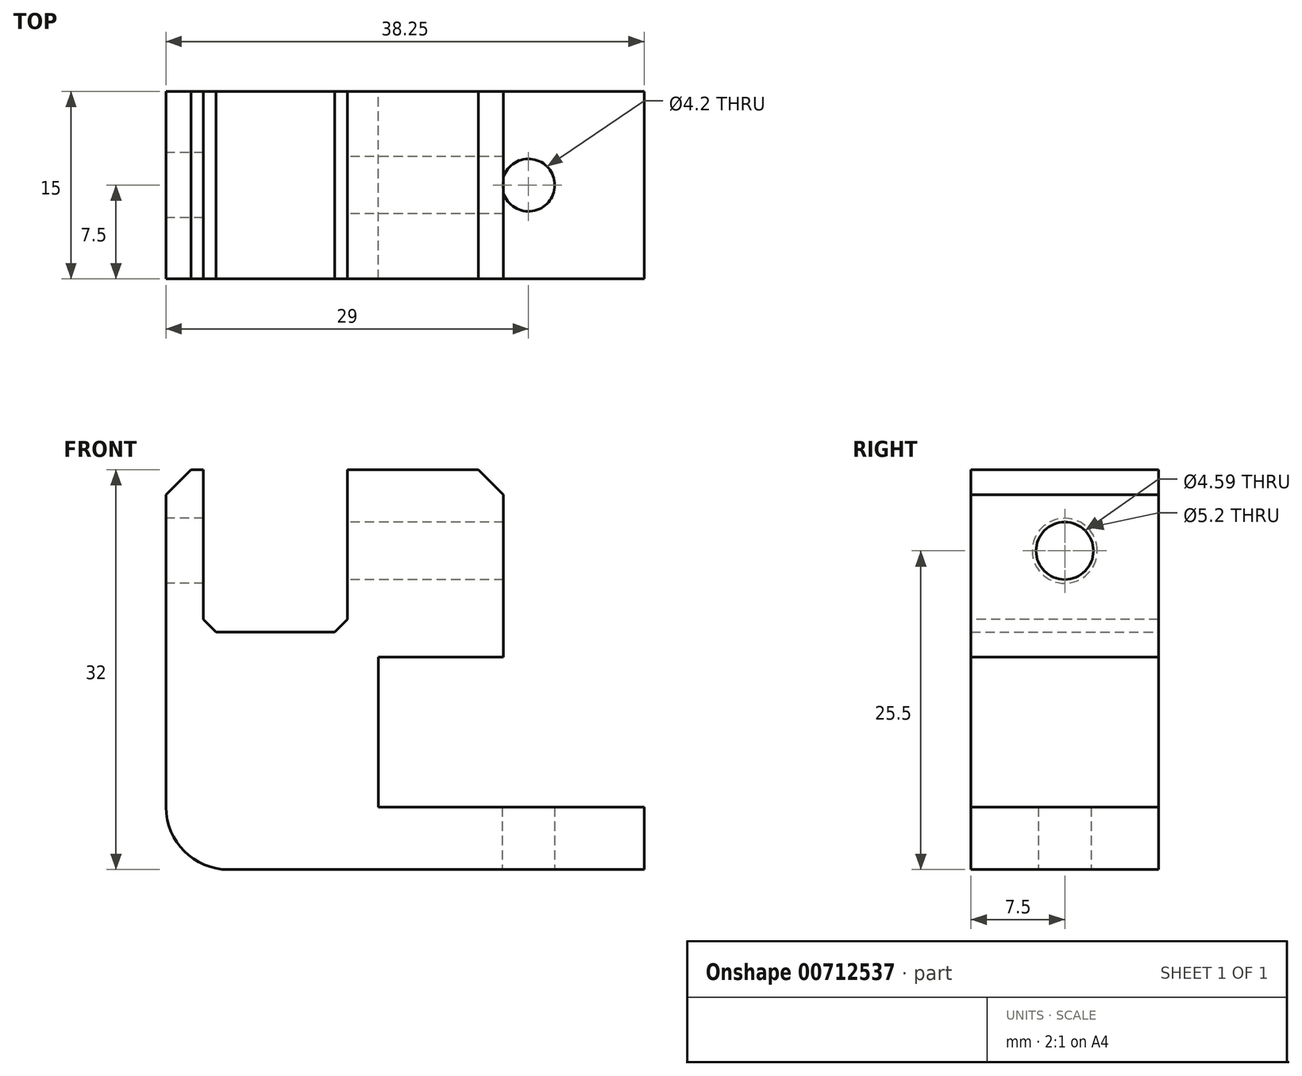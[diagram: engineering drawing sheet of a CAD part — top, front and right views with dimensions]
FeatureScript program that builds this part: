
annotation { "Feature Type Name" : "Feature", "Feature Type Description" : "" }
export const myFeature = defineFeature(function(context is Context, id is Id, definition is map)
    precondition{}
    {
        {
            var Q0;
            Q0=qCreatedBy(makeId("Front.planeOp"),FACE);
            var sketch = newSketch(context, id + "F0", { "sketchPlane" : qUnion([Q0])});
            skLineSegment(sketch, "E0", {"start": v(5, 0) * mm, "end": v(38.25, 0) * mm});
            skLineSegment(sketch, "E1", {"start": v(38.25, 0) * mm, "end": v(38.25, 5) * mm});
            skLineSegment(sketch, "E2", {"start": v(38.25, 5) * mm, "end": v(17, 5) * mm});
            skLineSegment(sketch, "E3", {"start": v(17, 5) * mm, "end": v(17, 17) * mm});
            skLineSegment(sketch, "E4", {"start": v(17, 17) * mm, "end": v(27, 17) * mm});
            skLineSegment(sketch, "E5", {"start": v(27, 17) * mm, "end": v(27, 32) * mm});
            skLineSegment(sketch, "E6", {"start": v(27, 32) * mm, "end": v(14.5, 32) * mm});
            skLineSegment(sketch, "E7", {"start": v(14.5, 32) * mm, "end": v(14.5, 19) * mm});
            skLineSegment(sketch, "E8", {"start": v(14.5, 19) * mm, "end": v(3, 19) * mm});
            skLineSegment(sketch, "E9", {"start": v(3, 19) * mm, "end": v(3, 32) * mm});
            skLineSegment(sketch, "E10", {"start": v(3, 32) * mm, "end": v(0, 32) * mm});
            skLineSegment(sketch, "E11", {"start": v(0, 32) * mm, "end": v(0, 5) * mm});
            skPoint(sketch, "E12.visualSharp", {"position": v(0, 0) * mm});
            skArc(sketch, "E12.filletArc", {"start": v(0, 5) * mm, "mid": v(1.46, 1.46) * mm, "end": v(5, 0) * mm});
            skSolve(sketch);
        }
        {
            var Q0;
            Q0=makeQuery(id+"F0.imprint","IMPRINT",FACE,{"disambiguationData":[TD([[makeQuery(id+"F0.imprint","IMPRINT",EDGE,{"derivedFrom":sQuery(id+"F0.wireOp",EDGE,"E0")}),1.0]])]});
            extrude(context, id + "F1", {"entities" : qUnion([Q0]), "depth" : 15 * mm, "offsetDistance" : 25 * mm});
        }
        {
            var Q0;
            Q0=makeQuery(id+"F1.opExtrude","SWEPT_FACE",FACE,{"disambiguationData":[OSD([sQuery(id+"F0.wireOp",EDGE,"E0")])]});
            var sketch = newSketch(context, id + "F2", { "sketchPlane" : qUnion([Q0])});
            skCircle(sketch, "E13", {"center": v(29, 7.5) * mm, "radius": 2.1 * mm});
            skSolve(sketch);
        }
        {
            var Q0;
            Q0=makeQuery(id+"F2.imprint","IMPRINT",FACE,{"disambiguationData":[TD([[makeQuery(id+"F2.imprint","IMPRINT",EDGE,{"derivedFrom":sQuery(id+"F2.wireOp",EDGE,"E13")}),1.0]])]});
            extrude(context, id + "F3", {"entities" : qUnion([Q0]), "operationType" : NewBodyOperationType.REMOVE, "endBound" : BoundingType.UP_TO_NEXT, "oppositeDirection" : true, "depth" : 25 * mm, "offsetDistance" : 25 * mm});
        }
        {
            var Q0;
            Q0=makeQuery(id+"F1.opExtrude","SWEPT_FACE",FACE,{"disambiguationData":[OSD([sQuery(id+"F0.wireOp",EDGE,"E11")])]});
            var sketch = newSketch(context, id + "F4", { "sketchPlane" : qUnion([Q0])});
            skCircle(sketch, "E14", {"center": v(7.5, 25.5) * mm, "radius": 2.3 * mm});
            skSolve(sketch);
        }
        {
            var Q0;
            Q0=makeQuery(id+"F4.imprint","IMPRINT",FACE,{"disambiguationData":[TD([[makeQuery(id+"F4.imprint","IMPRINT",EDGE,{"derivedFrom":sQuery(id+"F4.wireOp",EDGE,"E14")}),1.0]])]});
            extrude(context, id + "F5", {"entities" : qUnion([Q0]), "operationType" : NewBodyOperationType.REMOVE, "endBound" : BoundingType.THROUGH_ALL, "oppositeDirection" : true, "depth" : 25 * mm, "offsetDistance" : 25 * mm});
        }
        {
            var Q0;
            Q0=makeQuery(id+"F1.opExtrude","SWEPT_FACE",FACE,{"disambiguationData":[OSD([sQuery(id+"F0.wireOp",EDGE,"E11")])]});
            var sketch = newSketch(context, id + "F6", { "sketchPlane" : qUnion([Q0])});
            skCircle(sketch, "E15", {"center": v(7.5, 25.5) * mm, "radius": 2.6 * mm});
            skSolve(sketch);
        }
        {
            var Q0;
            Q0=makeQuery(id+"F6.imprint","IMPRINT",FACE,{"disambiguationData":[TD([[makeQuery(id+"F6.imprint","IMPRINT",EDGE,{"derivedFrom":sQuery(id+"F6.wireOp",EDGE,"E15")}),1.0]])]});
            extrude(context, id + "F7", {"entities" : qUnion([Q0]), "operationType" : NewBodyOperationType.REMOVE, "endBound" : BoundingType.UP_TO_NEXT, "oppositeDirection" : true, "depth" : 25 * mm, "offsetDistance" : 25 * mm});
        }
        {
            var Q0;
            Q0=makeQuery(id+"F1.opExtrude","SWEPT_EDGE",EDGE,{"disambiguationData":[OSD([sQuery(id+"F0.wireOp",EDGE,"E5"),sQuery(id+"F0.wireOp",EDGE,"E6")])]});
            var Q1;
            Q1=makeQuery(id+"F1.opExtrude","SWEPT_EDGE",EDGE,{"disambiguationData":[OSD([sQuery(id+"F0.wireOp",EDGE,"E10"),sQuery(id+"F0.wireOp",EDGE,"E11")])]});
            chamfer(context, id + "F8", {"entities" : qUnion([Q0, Q1]), "width" : 2 * mm, "tangentPropagation" : true});
        }
        {
            var Q0;
            Q0=makeQuery(id+"F1.opExtrude","SWEPT_EDGE",EDGE,{"disambiguationData":[OSD([sQuery(id+"F0.wireOp",EDGE,"E8"),sQuery(id+"F0.wireOp",EDGE,"E9")])]});
            var Q1;
            Q1=makeQuery(id+"F1.opExtrude","SWEPT_EDGE",EDGE,{"disambiguationData":[OSD([sQuery(id+"F0.wireOp",EDGE,"E7"),sQuery(id+"F0.wireOp",EDGE,"E8")])]});
            chamfer(context, id + "F9", {"entities" : qUnion([Q0, Q1]), "width" : 1 * mm, "tangentPropagation" : true});
        }
    });
